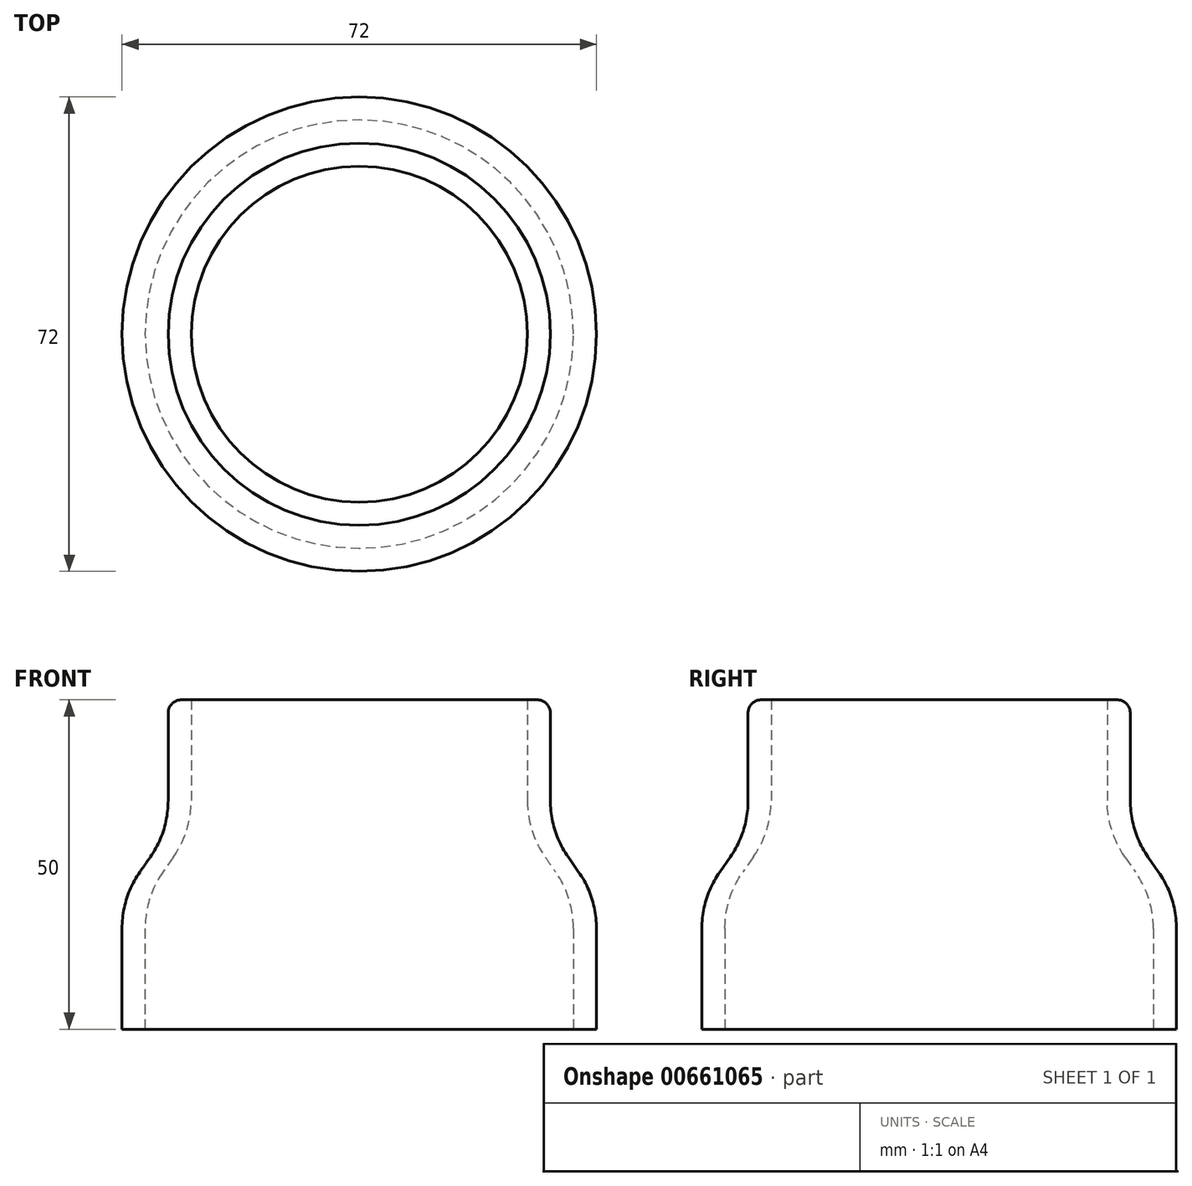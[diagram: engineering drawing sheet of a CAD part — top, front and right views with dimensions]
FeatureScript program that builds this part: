
annotation { "Feature Type Name" : "Feature", "Feature Type Description" : "" }
export const myFeature = defineFeature(function(context is Context, id is Id, definition is map)
    precondition{}
    {
        {
            var Q0;
            Q0=qCreatedBy(makeId("Front.planeOp"),FACE);
            var sketch = newSketch(context, id + "F0", { "sketchPlane" : qUnion([Q0])});
            skLineSegment(sketch, "E0", {"start": v(0, 0) * mm, "end": v(0, 25) * mm, "construction": true});
            skLineSegment(sketch, "E1", {"start": v(0, 0) * mm, "end": v(0, -25) * mm, "construction": true});
            skLineSegment(sketch, "E2", {"start": v(0, -25) * mm, "end": v(-32.5, -25) * mm, "construction": true});
            skLineSegment(sketch, "E3", {"start": v(-32.5, -25) * mm, "end": v(-36, -25) * mm});
            skLineSegment(sketch, "E4", {"start": v(-32.5, -25) * mm, "end": v(-32.5, -5) * mm});
            skLineSegment(sketch, "E5", {"start": v(-36, -25) * mm, "end": v(-36, -5) * mm});
            skLineSegment(sketch, "E6", {"start": v(0, 25) * mm, "end": v(-25.5, 25) * mm, "construction": true});
            skLineSegment(sketch, "E7", {"start": v(-25.5, 25) * mm, "end": v(-29, 25) * mm});
            skLineSegment(sketch, "E8", {"start": v(-25.5, 25) * mm, "end": v(-25.5, 5) * mm});
            skLineSegment(sketch, "E9", {"start": v(-29, 25) * mm, "end": v(-29, 5) * mm});
            skLineSegment(sketch, "E10", {"start": v(-29, 5) * mm, "end": v(-36, -5) * mm});
            skLineSegment(sketch, "E11", {"start": v(-25.5, 5) * mm, "end": v(-32.5, -5) * mm});
            skSolve(sketch);
        }
        {
            var Q0;
            Q0=makeQuery(id+"F0.imprint","IMPRINT",FACE,{"disambiguationData":[TD([[makeQuery(id+"F0.imprint","IMPRINT",EDGE,{"derivedFrom":sQuery(id+"F0.wireOp",EDGE,"E3")}),-1.0]])]});
            var Q1;
            Q1=sQuery(id+"F0.wireOp",EDGE,"E0");
            revolve(context, id + "F1", {"entities" : qUnion([Q0]), "axis" : qUnion([Q1]), "revolveType" : RevolveType.FULL});
        }
        {
            var Q0;
            Q0=makeQuery(id+"F1.opRevolve","SWEPT_EDGE",EDGE,{"disambiguationData":[OSD([sQuery(id+"F0.wireOp",EDGE,"E9"),sQuery(id+"F0.wireOp",EDGE,"E10")])]});
            var Q1;
            Q1=makeQuery(id+"F1.opRevolve","SWEPT_EDGE",EDGE,{"disambiguationData":[OSD([sQuery(id+"F0.wireOp",EDGE,"E5"),sQuery(id+"F0.wireOp",EDGE,"E10")])]});
            var Q2;
            Q2=makeQuery(id+"F1.opRevolve","SWEPT_EDGE",EDGE,{"disambiguationData":[OSD([sQuery(id+"F0.wireOp",EDGE,"E8"),sQuery(id+"F0.wireOp",EDGE,"E11")])]});
            var Q3;
            Q3=makeQuery(id+"F1.opRevolve","SWEPT_EDGE",EDGE,{"disambiguationData":[OSD([sQuery(id+"F0.wireOp",EDGE,"E4"),sQuery(id+"F0.wireOp",EDGE,"E11")])]});
            fillet(context, id + "F2", {"entities" : qUnion([Q0, Q1, Q2, Q3]), "radius" : 15 * mm, "tangentPropagation" : true, "allowEdgeOverflow" : false});
        }
        {
            var Q0;
            Q0=makeQuery(id+"F1.opRevolve","SWEPT_EDGE",EDGE,{"disambiguationData":[OSD([sQuery(id+"F0.wireOp",EDGE,"E7"),sQuery(id+"F0.wireOp",EDGE,"E9")])]});
            fillet(context, id + "F3", {"entities" : qUnion([Q0]), "radius" : 2 * mm, "tangentPropagation" : true, "allowEdgeOverflow" : false});
        }
    });
